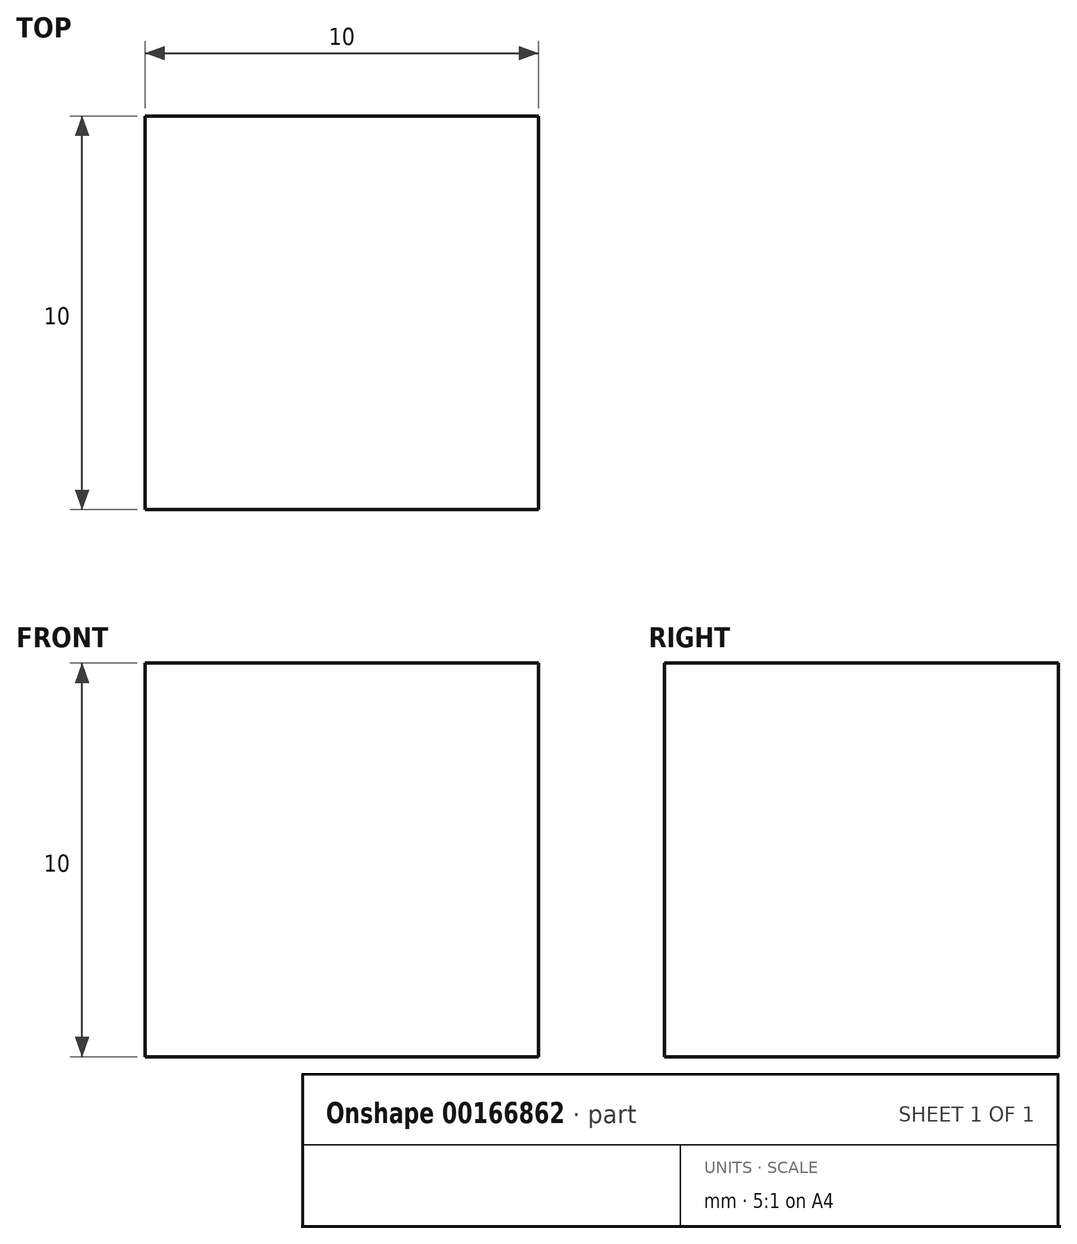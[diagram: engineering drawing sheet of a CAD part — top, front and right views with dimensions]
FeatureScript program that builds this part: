
annotation { "Feature Type Name" : "Feature", "Feature Type Description" : "" }
export const myFeature = defineFeature(function(context is Context, id is Id, definition is map)
    precondition{}
    {
        {
            var Q0;
            Q0=qCreatedBy(makeId("Top.planeOp"),FACE);
            var sketch = newSketch(context, id + "F0", { "sketchPlane" : qUnion([Q0])});
            skLineSegment(sketch, "E0.bottom", {"start": v(5, -5) * mm, "end": v(-5, -5) * mm});
            skLineSegment(sketch, "E0.top", {"start": v(5, 5) * mm, "end": v(-5, 5) * mm});
            skLineSegment(sketch, "E0.left", {"start": v(5, -5) * mm, "end": v(5, 5) * mm});
            skLineSegment(sketch, "E0.right", {"start": v(-5, -5) * mm, "end": v(-5, 5) * mm});
            skPoint(sketch, "E0.middle", {"position": v(0, 0) * mm});
            skSolve(sketch);
        }
        {
            var Q0;
            Q0=makeQuery(id+"F0.imprint","IMPRINT",FACE,{"disambiguationData":[TD([[makeQuery(id+"F0.imprint","IMPRINT",EDGE,{"derivedFrom":sQuery(id+"F0.wireOp",EDGE,"E0.bottom")}),-1.0]])]});
            extrude(context, id + "F1", {"entities" : qUnion([Q0]), "depth" : 5 * mm, "hasSecondDirection" : true, "secondDirectionOppositeDirection" : true, "secondDirectionDepth" : 5 * mm});
        }
    });
